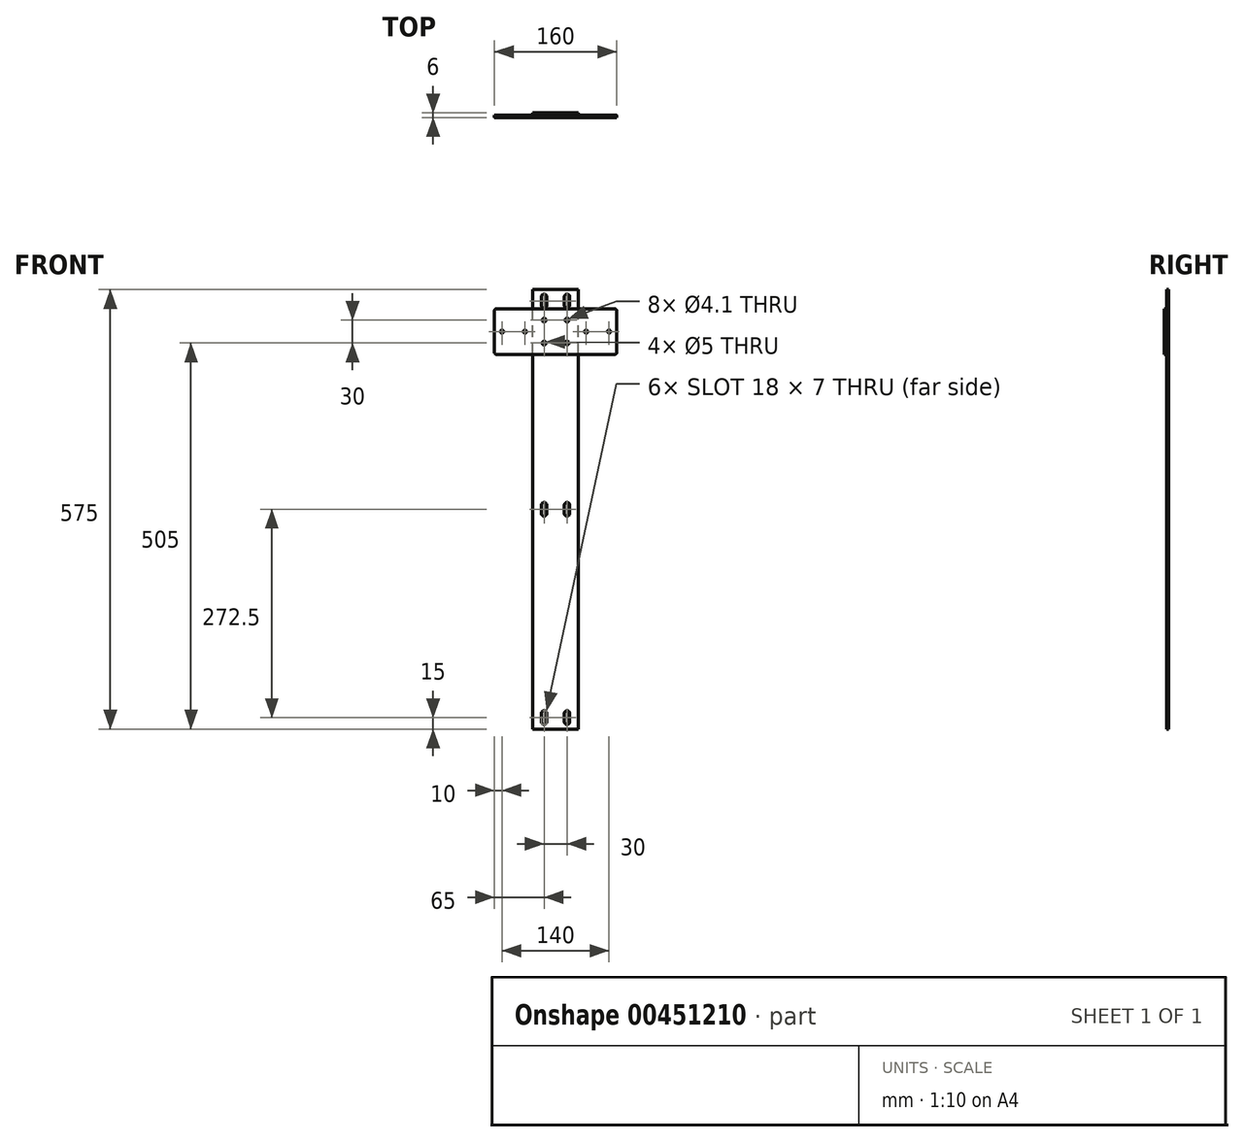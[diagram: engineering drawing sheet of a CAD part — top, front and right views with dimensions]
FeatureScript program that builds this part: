
annotation { "Feature Type Name" : "Feature", "Feature Type Description" : "" }
export const myFeature = defineFeature(function(context is Context, id is Id, definition is map)
    precondition{}
    {
        {
            var Q0;
            Q0=qCreatedBy(makeId("Front.planeOp"),FACE);
            var sketch = newSketch(context, id + "F0", { "sketchPlane" : qUnion([Q0])});
            skLineSegment(sketch, "E0.bottom", {"start": v(30, 0) * mm, "end": v(-30, 0) * mm});
            skLineSegment(sketch, "E0.top", {"start": v(30, 575) * mm, "end": v(-30, 575) * mm});
            skLineSegment(sketch, "E0.left", {"start": v(30, 0) * mm, "end": v(30, 575) * mm});
            skLineSegment(sketch, "E0.right", {"start": v(-30, 0) * mm, "end": v(-30, 575) * mm});
            skPoint(sketch, "E0.middle", {"position": v(0, 287.5) * mm});
            skCircle(sketch, "E1", {"center": v(-15, 535) * mm, "radius": 2.05 * mm});
            skCircle(sketch, "E2", {"center": v(-15, 505) * mm, "radius": 2.05 * mm});
            skCircle(sketch, "E3", {"center": v(15, 535) * mm, "radius": 2.05 * mm});
            skCircle(sketch, "E4", {"center": v(15, 505) * mm, "radius": 2.05 * mm});
            skLineSegment(sketch, "E5.bottom", {"start": v(-11.5, 554.5) * mm, "end": v(-18.5, 554.5) * mm, "construction": true});
            skLineSegment(sketch, "E5.top", {"start": v(-11.5, 565.5) * mm, "end": v(-18.5, 565.5) * mm, "construction": true});
            skLineSegment(sketch, "E5.left", {"start": v(-11.5, 554.5) * mm, "end": v(-11.5, 565.5) * mm});
            skLineSegment(sketch, "E5.right", {"start": v(-18.5, 554.5) * mm, "end": v(-18.5, 565.5) * mm});
            skPoint(sketch, "E5.middle", {"position": v(-15, 560) * mm});
            skArc(sketch, "E6", {"start": v(-11.5, 565.5) * mm, "mid": v(-15, 569) * mm, "end": v(-18.5, 565.5) * mm});
            skArc(sketch, "E7", {"start": v(-18.5, 554.5) * mm, "mid": v(-15, 551) * mm, "end": v(-11.5, 554.5) * mm});
            skLineSegment(sketch, "E8.bottom", {"start": v(18.5, 554.5) * mm, "end": v(11.5, 554.5) * mm, "construction": true});
            skLineSegment(sketch, "E8.top", {"start": v(18.5, 565.5) * mm, "end": v(11.5, 565.5) * mm, "construction": true});
            skLineSegment(sketch, "E8.left", {"start": v(18.5, 554.5) * mm, "end": v(18.5, 565.5) * mm});
            skLineSegment(sketch, "E8.right", {"start": v(11.5, 554.5) * mm, "end": v(11.5, 565.5) * mm});
            skPoint(sketch, "E8.middle", {"position": v(15, 560) * mm});
            skArc(sketch, "E9", {"start": v(18.5, 565.5) * mm, "mid": v(15, 569) * mm, "end": v(11.5, 565.5) * mm});
            skArc(sketch, "E10", {"start": v(11.5, 554.5) * mm, "mid": v(15, 551) * mm, "end": v(18.5, 554.5) * mm});
            skLineSegment(sketch, "E11.bottom", {"start": v(-11.5, 9.5) * mm, "end": v(-18.5, 9.5) * mm, "construction": true});
            skLineSegment(sketch, "E11.top", {"start": v(-11.5, 20.5) * mm, "end": v(-18.5, 20.5) * mm, "construction": true});
            skLineSegment(sketch, "E11.left", {"start": v(-11.5, 9.5) * mm, "end": v(-11.5, 20.5) * mm});
            skLineSegment(sketch, "E11.right", {"start": v(-18.5, 9.5) * mm, "end": v(-18.5, 20.5) * mm});
            skPoint(sketch, "E11.middle", {"position": v(-15, 15) * mm});
            skArc(sketch, "E12", {"start": v(-11.5, 20.5) * mm, "mid": v(-15, 24) * mm, "end": v(-18.5, 20.5) * mm});
            skArc(sketch, "E13", {"start": v(-18.5, 9.5) * mm, "mid": v(-15, 6) * mm, "end": v(-11.5, 9.5) * mm});
            skLineSegment(sketch, "E14.bottom", {"start": v(18.5, 9.5) * mm, "end": v(11.5, 9.5) * mm, "construction": true});
            skLineSegment(sketch, "E14.top", {"start": v(18.5, 20.5) * mm, "end": v(11.5, 20.5) * mm, "construction": true});
            skLineSegment(sketch, "E14.left", {"start": v(18.5, 9.5) * mm, "end": v(18.5, 20.5) * mm});
            skLineSegment(sketch, "E14.right", {"start": v(11.5, 9.5) * mm, "end": v(11.5, 20.5) * mm});
            skPoint(sketch, "E14.middle", {"position": v(15, 15) * mm});
            skArc(sketch, "E15", {"start": v(18.5, 20.5) * mm, "mid": v(15, 24) * mm, "end": v(11.5, 20.5) * mm});
            skArc(sketch, "E16", {"start": v(11.5, 9.5) * mm, "mid": v(15, 6) * mm, "end": v(18.5, 9.5) * mm});
            skLineSegment(sketch, "E17.bottom", {"start": v(-11.5, 282) * mm, "end": v(-18.5, 282) * mm, "construction": true});
            skLineSegment(sketch, "E17.top", {"start": v(-11.5, 293) * mm, "end": v(-18.5, 293) * mm, "construction": true});
            skLineSegment(sketch, "E17.left", {"start": v(-11.5, 282) * mm, "end": v(-11.5, 293) * mm});
            skLineSegment(sketch, "E17.right", {"start": v(-18.5, 282) * mm, "end": v(-18.5, 293) * mm});
            skPoint(sketch, "E17.middle", {"position": v(-15, 287.5) * mm});
            skArc(sketch, "E18", {"start": v(-11.5, 293) * mm, "mid": v(-15, 296.5) * mm, "end": v(-18.5, 293) * mm});
            skArc(sketch, "E19", {"start": v(-18.5, 282) * mm, "mid": v(-15, 278.5) * mm, "end": v(-11.5, 282) * mm});
            skLineSegment(sketch, "E20.bottom", {"start": v(18.5, 282) * mm, "end": v(11.5, 282) * mm, "construction": true});
            skLineSegment(sketch, "E20.top", {"start": v(18.5, 293) * mm, "end": v(11.5, 293) * mm, "construction": true});
            skLineSegment(sketch, "E20.left", {"start": v(18.5, 282) * mm, "end": v(18.5, 293) * mm});
            skLineSegment(sketch, "E20.right", {"start": v(11.5, 282) * mm, "end": v(11.5, 293) * mm});
            skPoint(sketch, "E20.middle", {"position": v(15, 287.5) * mm});
            skArc(sketch, "E21", {"start": v(18.5, 293) * mm, "mid": v(15, 296.5) * mm, "end": v(11.5, 293) * mm});
            skArc(sketch, "E22", {"start": v(11.5, 282) * mm, "mid": v(15, 278.5) * mm, "end": v(18.5, 282) * mm});
            skSolve(sketch);
        }
        {
            var Q0;
            Q0 = qSketchRegion(id + "F0", true);
            extrude(context, id + "F1", {"entities" : qUnion([Q0]), "depth" : 3 * mm, "offsetDistance" : 25 * mm});
        }
        {
            var Q0;
            Q0=makeQuery(id+"F1.opExtrude","CAP_FACE",FACE,{"disambiguationData":[OSD([sQuery(id+"F0.wireOp",EDGE,"E0.bottom"),sQuery(id+"F0.wireOp",EDGE,"E0.top"),sQuery(id+"F0.wireOp",EDGE,"E0.left"),sQuery(id+"F0.wireOp",EDGE,"E0.right"),sQuery(id+"F0.wireOp",EDGE,"E1"),sQuery(id+"F0.wireOp",EDGE,"E2"),sQuery(id+"F0.wireOp",EDGE,"E3"),sQuery(id+"F0.wireOp",EDGE,"E4"),sQuery(id+"F0.wireOp",EDGE,"E5.left"),sQuery(id+"F0.wireOp",EDGE,"E5.right"),sQuery(id+"F0.wireOp",EDGE,"E6"),sQuery(id+"F0.wireOp",EDGE,"E7"),sQuery(id+"F0.wireOp",EDGE,"E8.left"),sQuery(id+"F0.wireOp",EDGE,"E8.right"),sQuery(id+"F0.wireOp",EDGE,"E9"),sQuery(id+"F0.wireOp",EDGE,"E10"),sQuery(id+"F0.wireOp",EDGE,"E11.left"),sQuery(id+"F0.wireOp",EDGE,"E11.right"),sQuery(id+"F0.wireOp",EDGE,"E12"),sQuery(id+"F0.wireOp",EDGE,"E13"),sQuery(id+"F0.wireOp",EDGE,"E14.left"),sQuery(id+"F0.wireOp",EDGE,"E14.right"),sQuery(id+"F0.wireOp",EDGE,"E15"),sQuery(id+"F0.wireOp",EDGE,"E16")])],"isStart":false});
            var sketch = newSketch(context, id + "F2", { "sketchPlane" : qUnion([Q0])});
            skLineSegment(sketch, "E23.bottom", {"start": v(80, 490) * mm, "end": v(-80, 490) * mm});
            skLineSegment(sketch, "E23.top", {"start": v(80, 550) * mm, "end": v(-80, 550) * mm});
            skLineSegment(sketch, "E23.left", {"start": v(80, 490) * mm, "end": v(80, 550) * mm});
            skLineSegment(sketch, "E23.right", {"start": v(-80, 490) * mm, "end": v(-80, 550) * mm});
            skPoint(sketch, "E23.middle", {"position": v(0, 520) * mm});
            skPoint(sketch, "E24", {"position": v(0, 575) * mm});
            skLineSegment(sketch, "E25", {"start": v(-80, 520) * mm, "end": v(80, 520) * mm, "construction": true});
            skCircle(sketch, "E26", {"center": v(-15, 535) * mm, "radius": 2.5 * mm});
            skCircle(sketch, "E27", {"center": v(15, 535) * mm, "radius": 2.5 * mm});
            skCircle(sketch, "E28", {"center": v(15, 505) * mm, "radius": 2.5 * mm});
            skCircle(sketch, "E29", {"center": v(-15, 505) * mm, "radius": 2.5 * mm});
            skCircle(sketch, "E30", {"center": v(70, 520) * mm, "radius": 2.05 * mm});
            skCircle(sketch, "E31", {"center": v(40, 520) * mm, "radius": 2.05 * mm});
            skLineSegment(sketch, "E32", {"start": v(0, 520) * mm, "end": v(0, 528.46) * mm, "construction": true});
            skCircle(sketch, "E33.MirrorC", {"center": v(-70, 520) * mm, "radius": 2.05 * mm});
            skCircle(sketch, "E34.MirrorC", {"center": v(-40, 520) * mm, "radius": 2.05 * mm});
            skSolve(sketch);
        }
        {
            var Q0;
            Q0 = qSketchRegion(id + "F2", true);
            extrude(context, id + "F3", {"entities" : qUnion([Q0]), "depth" : 3 * mm, "offsetDistance" : 25 * mm});
        }
        {
            var Q0;
            Q0=makeQuery(id+"F3.opExtrude","SWEPT_EDGE",EDGE,{"disambiguationData":[OSD([sQuery(id+"F2.wireOp",EDGE,"E23.top"),sQuery(id+"F2.wireOp",EDGE,"E23.right")])]});
            var Q1;
            Q1=makeQuery(id+"F3.opExtrude","SWEPT_EDGE",EDGE,{"disambiguationData":[OSD([sQuery(id+"F2.wireOp",EDGE,"E23.bottom"),sQuery(id+"F2.wireOp",EDGE,"E23.right")])]});
            var Q2;
            Q2=makeQuery(id+"F3.opExtrude","SWEPT_EDGE",EDGE,{"disambiguationData":[OSD([sQuery(id+"F2.wireOp",EDGE,"E23.top"),sQuery(id+"F2.wireOp",EDGE,"E23.left")])]});
            var Q3;
            Q3=makeQuery(id+"F3.opExtrude","SWEPT_EDGE",EDGE,{"disambiguationData":[OSD([sQuery(id+"F2.wireOp",EDGE,"E23.bottom"),sQuery(id+"F2.wireOp",EDGE,"E23.left")])]});
            fillet(context, id + "F4", {"entities" : qUnion([Q0, Q1, Q2, Q3]), "tangentPropagation" : true, "radius" : 3 * mm, "defaultsChanged" : true, "vertexSettings" : [], "allowEdgeOverflow" : false});
        }
    });
